# Revit family: ECOflo_EC230-600_LOD200
name_source: partatom
category: Mechanical Equipment
revit_build: Autodesk Revit 2014 (Build: 20130308_1515(x64)
units: mm (PartAtom-declared; Revit-internal decimal feet)

## types (1)
- Direct Gas Fired Water Storage Heater 230/600
    6 Monthly = Maintenance tasks or SFG2012 codes. If Not Applicable Mark '0'
    Access Clearance Bottom = 0 mm
    Access Clearance Front = 1000 mm
    Access Clearance Left = 100 mm
    Access Clearance Rear = 100 mm
    Access Clearance Right = 500 mm
    Access Clearance Top = 450 mm
    Air Inlet Connection Radius = 50 mm
    Air Inlet Connection Size = 100 mm
    Air Inlet Connection Type = External
    Annually = Maintenance tasks or SFG2012 codes. If Not Applicable Mark '0'
    Assembly Code = D3010
    BMS Links = Yes
    Bespoke Timeframe = Maintenance tasks or SFG2012 codes. If Not Applicable Mark '0'
    CE Approval = Yes - 0063BP3567
    Clean Out and Inspection Opening Type = Flanged
    Cold Water Outlet = 38 mm
    Cold Water Outlet Radius = 19 mm
    Colour = Black & Grey (RAL 7047)
    Condensate Drain Radius = 20 mm
    Condensate Drain Size = 40 mm
    Condensing = Yes
    Continuous Output at 44 Degree Differential l/h = 684
    Continuous Output at 50 Degree Differential l/h = 602
    Control ThermostatRange = 5 °C
    Control Type = Internal
    Daily = Maintenance tasks or SFG2012 codes. If Not Applicable Mark '0'
    Description = Condensing Storage Water Heater
    Drain Connection Radus = 10 mm
    Drain Connection Size = 19 mm
    Drain Connection Type = Socket
    Efficiency (Gross) (%) = 98
    Embodied Carbon kgCO2e = University of Bath ICE Data if none other available
    Emissions mg/kWh = 44
    Enclosure Rating = 20
    Energy Technology List = Yes
    Environmental Product Declaration = 3rd Party Verification
    ErP Energy Label = Yes
    External Material = Aluminium
    Finish = Painted
    Flow and Return Connection Radius = 19 mm
    Flow and Return Connection Size = 38 mm
    Flow and Return Connection Type = Threaded
    Flue Connection Radius = 75 mm
    Flue Connection Size = 150 mm
    Flue Connection Type = External
    Flue or Air Intake Classification = B23, C13, C33 & C53
    Frequency = 50 Hz
    Fuel = Gas - NG
    Fuel Connection Radius = 10 mm
    Fuel Connection Size = 19 mm
    Fuel Connection Type = Threaded
    Full Load Current = 3 A
    Fuse Rating = 5 A
    Gas Consumption rate = 3.4 m³/h
    Gas Flow Rate = 3.4 m³/h
    Green Guide for Specification = A - E
    Gross Input Of Appliance = 37 kW
    Gross Weight = 450.00 kg
    Heat Exchanger Material = Steel Glass Lined
    Heat Generator Efficiency = 96%
    Heat Loss kWh/24h = 5.59
    Heat Up Time mins = 23
    Hot Water Outlet = 38 mm
    Hot Water Outlet Radius = 19 mm
    Hot Water Recovery (Thru 50ºC) (Litres/Hour) = 980
    Insulation Thickness = 50 mm
    Insulation Type = Foam Injected
    Interlocks = Yes
    Life Cycle Analysis = BREEAM
    Load Sub-Classification Motor = Yes
    Location of Manufacturer-GridRef = Northing,Easting
    Maintenance Required 0-300hrs = Maintenance tasks required during this time frame. If Not Applicable Mark '0'
    Maintenance Required 1001-2000hrs = Maintenance tasks required during this time frame. If Not Applicable Mark '0'
    Maintenance Required 2001-4000hrs = Maintenance tasks required during this time frame. If Not Applicable Mark '0'
    Maintenance Required 40001-8000hrs = Maintenance tasks required during this time frame. If Not Applicable Mark '0'
    Maintenance Required 601-1000hrs = Maintenance tasks required during this time frame. If Not Applicable Mark '0'
    Maintenance Required 8001-12000hrs = Maintenance tasks required during this time frame. If Not Applicable Mark '0'
    Manufacturer = Andrews Water Heaters
    Max Operating Pressure When Open Vented = 10.3 bar
    Max Operating Pressure When Unvented = 3.5 bar
    Maximum Gas Inlet Pressure mbar = 40 mbar
    Maximum Oil Inlet Pressure mbar = 0
    Maximum Power Consumption = 120 W
    Maximum Starting Current = 4 A
    Maximum Water Temperature = 70 °C
    Min Operating Pressure mbar = 1
    Minimum Gas Inlet Pressure mbar = 18
    Minimum Oil Inlet Pressure mbar = 0
    Minimum Power Consumption = 120 W
    Model = EC230/600
    Monthly = Maintenance tasks required during this time frame. If Not Applicable Mark '0'
    Mounting = Floor Standing
    Nett Weight = 259.00 kg
    Nominal Gas Inlet Pressure = 21 mbar
    Nominal Oil Inlet Pressure mbar = 0
    Number of Poles = 1
    O&M Manual = http://www.andrewswaterheaters.co.uk
    Oil Consumption Rate l/h = 0
    Oil Flow Rate kg/h = 0
    Operation = On/Off
    Overall Diameter = 718 mm
    Overall Height = 1448 mm
    Overall Length = 0 mm
    Overall Width = 0 mm
    Power Connector = Yes
    Power Consumption (W) = 210
    Power Consumption of Shunt Pump = 0 W
    Product Literature = http://www.andrewswaterheaters.co.uk
    Product Range = ECOflo
    Quarterly = Maintenance tasks or SFG2012 codes. If Not Applicable Mark '0'
    Recovery Rate litre/min = 10
    Reference Standard = BSE 89
    Responsible Extraction of Materials = Yes
    Responsible Sourcing of Materials = Endorsing Body
    Safety Valve Connection Size = 28 mm
    Safety Valve Connection Type = Threaded
    Secondary Return Connection Radius = 10 mm
    Secondary Return Connection Size = 19 mm
    Secondary Return Connection Type = Socket
    Shape = Cylindrical (Vertical)
    Shipping Carton Height = 1664 mm
    Shipping Carton Length = 889 mm
    Shipping Carton Width = 819 mm
    Shipping Weight = 259.00 kg
    Storage Capacity = 230.000 L
    Supply Phase = Single Phase
    Type = Direct Gas Fired Water Storage Heater
    Type Comments = Forced Draught Premix Condensing
    URL = http://www.andrewswaterheaters.co.uk
    Voltage = 240 V
    Weekly = Maintenance tasks or SFG2012 codes. If Not Applicable Mark '0'
    Weight (Full) (kg) = 788

## geometry (parser evidence)
native form markers: Blend x38, Extrusion x1, Sweep x4
no freeform markers — native parametric forms only
